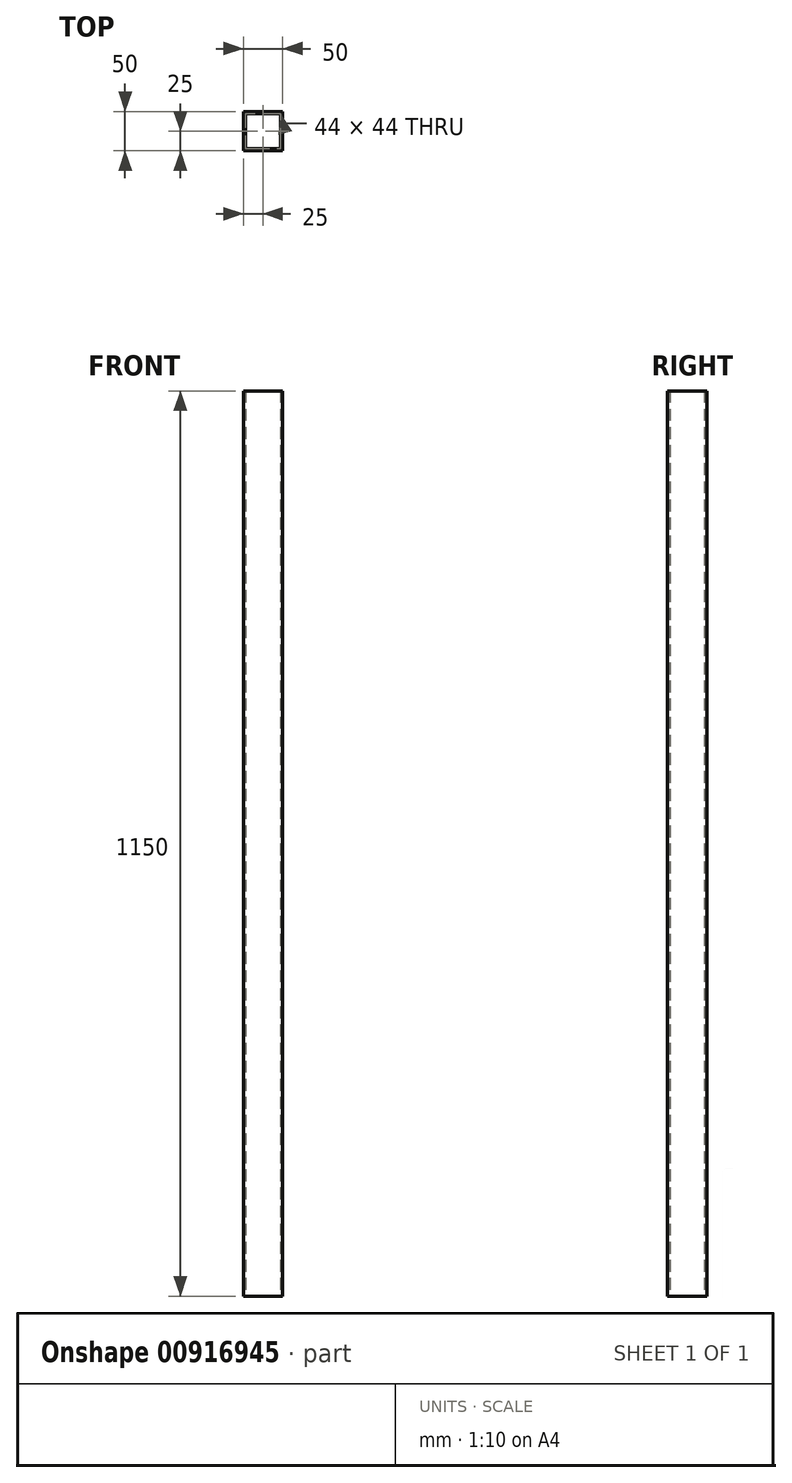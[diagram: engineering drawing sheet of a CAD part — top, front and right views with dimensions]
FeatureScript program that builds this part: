
annotation { "Feature Type Name" : "Feature", "Feature Type Description" : "" }
export const myFeature = defineFeature(function(context is Context, id is Id, definition is map)
    precondition{}
    {
        {
            var Q0;
            Q0=qCreatedBy(makeId("Top.planeOp"),FACE);
            var sketch = newSketch(context, id + "F0", { "sketchPlane" : qUnion([Q0])});
            skLineSegment(sketch, "E0.bottom", {"start": v(0, 0) * mm, "end": v(50, 0) * mm});
            skLineSegment(sketch, "E0.top", {"start": v(0, 50) * mm, "end": v(50, 50) * mm});
            skLineSegment(sketch, "E0.left", {"start": v(0, 0) * mm, "end": v(0, 50) * mm});
            skLineSegment(sketch, "E0.right", {"start": v(50, 0) * mm, "end": v(50, 50) * mm});
            skLineSegment(sketch, "E1.0", {"start": v(3, 3) * mm, "end": v(47, 3) * mm});
            skLineSegment(sketch, "E1.1", {"start": v(3, 3) * mm, "end": v(3, 47) * mm});
            skLineSegment(sketch, "E1.2", {"start": v(3, 47) * mm, "end": v(47, 47) * mm});
            skLineSegment(sketch, "E1.3", {"start": v(47, 3) * mm, "end": v(47, 47) * mm});
            skSolve(sketch);
        }
        {
            var Q0;
            Q0=makeQuery(id+"F0.imprint","IMPRINT",FACE,{"disambiguationData":[TD([[makeQuery(id+"F0.imprint","IMPRINT",EDGE,{"derivedFrom":sQuery(id+"F0.wireOp",EDGE,"E0.bottom")}),1.0]])]});
            extrude(context, id + "F1", {"entities" : qUnion([Q0]), "depth" : 1150 * mm, "offsetDistance" : 25 * mm});
        }
    });
